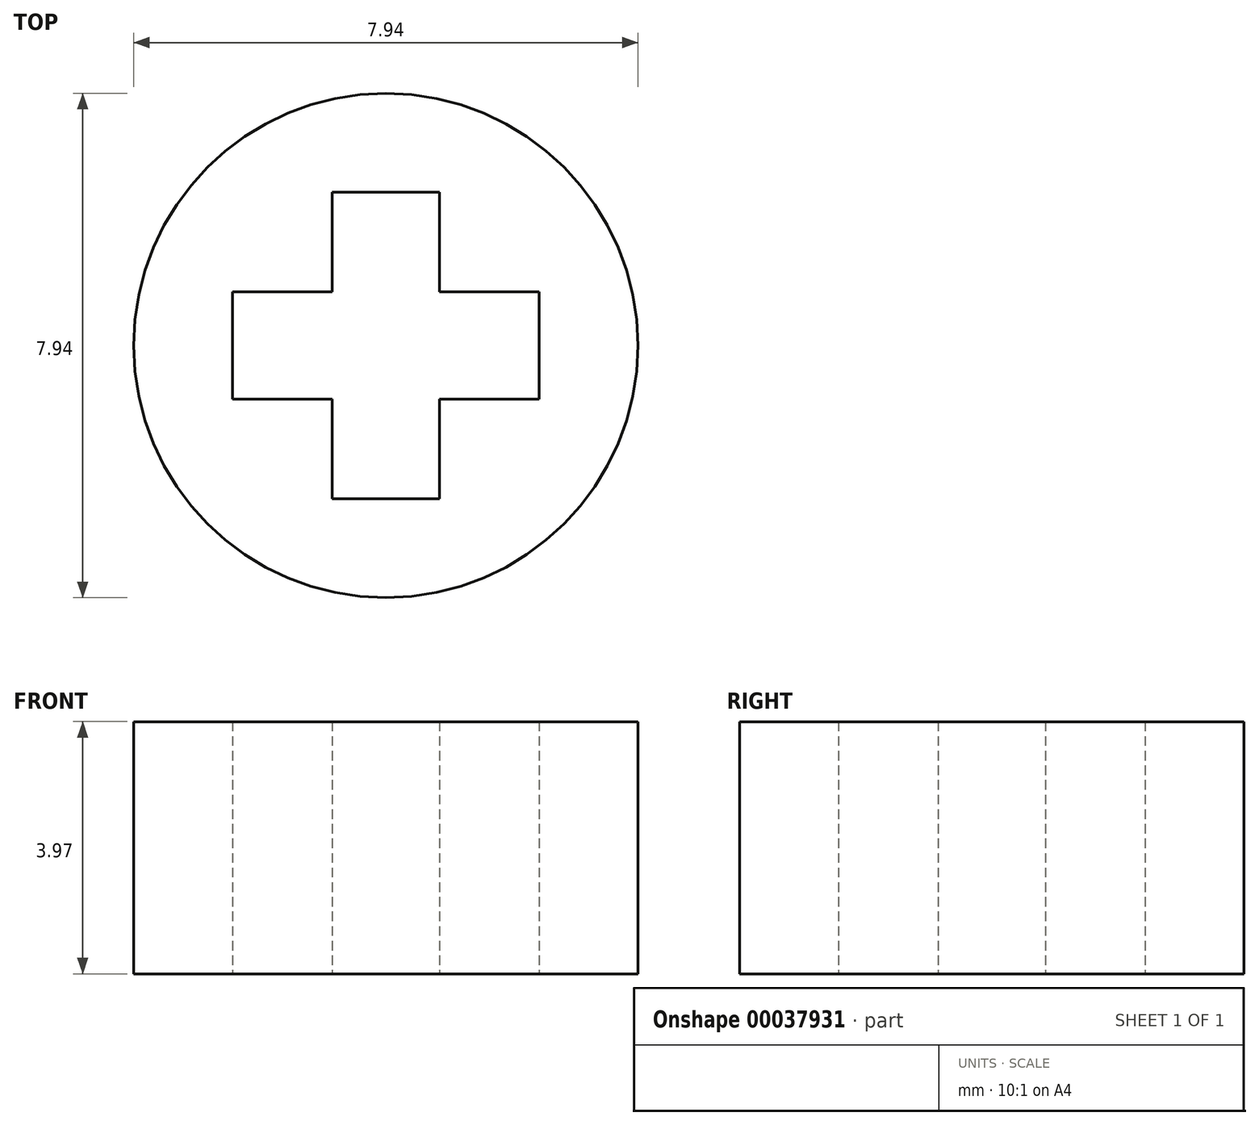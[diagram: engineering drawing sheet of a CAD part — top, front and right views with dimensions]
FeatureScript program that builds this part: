
annotation { "Feature Type Name" : "Feature", "Feature Type Description" : "" }
export const myFeature = defineFeature(function(context is Context, id is Id, definition is map)
    precondition{}
    {
        {
            var Q0;
            Q0=qCreatedBy(makeId("Top.planeOp"),FACE);
            var sketch = newSketch(context, id + "F0", { "sketchPlane" : qUnion([Q0])});
            skCircle(sketch, "E0", {"center": v(0, 0) * mm, "radius": 3.97 * mm});
            skLineSegment(sketch, "E1.rect.bottom", {"start": v(2.41, 0.84) * mm, "end": v(-2.41, 0.84) * mm});
            skLineSegment(sketch, "E1.rect.top", {"start": v(2.41, -0.84) * mm, "end": v(-2.41, -0.84) * mm});
            skLineSegment(sketch, "E1.rect.left", {"start": v(2.41, 0.84) * mm, "end": v(2.41, -0.84) * mm});
            skLineSegment(sketch, "E1.rect.right", {"start": v(-2.41, 0.84) * mm, "end": v(-2.41, -0.84) * mm});
            skLineSegment(sketch, "E2.rect.bottom", {"start": v(0.84, -2.41) * mm, "end": v(-0.84, -2.41) * mm});
            skLineSegment(sketch, "E2.rect.top", {"start": v(0.84, 2.41) * mm, "end": v(-0.84, 2.41) * mm});
            skLineSegment(sketch, "E2.rect.left", {"start": v(0.84, -2.41) * mm, "end": v(0.84, 2.41) * mm});
            skLineSegment(sketch, "E2.rect.right", {"start": v(-0.84, -2.41) * mm, "end": v(-0.84, 2.41) * mm});
            skSolve(sketch);
        }
        {
            var Q0;
            Q0=qSketchRegion(id+"F0",true);
            extrude(context, id + "F1", {"entities" : qUnion([Q0]), "depth" : 3.97 * mm});
        }
    });
